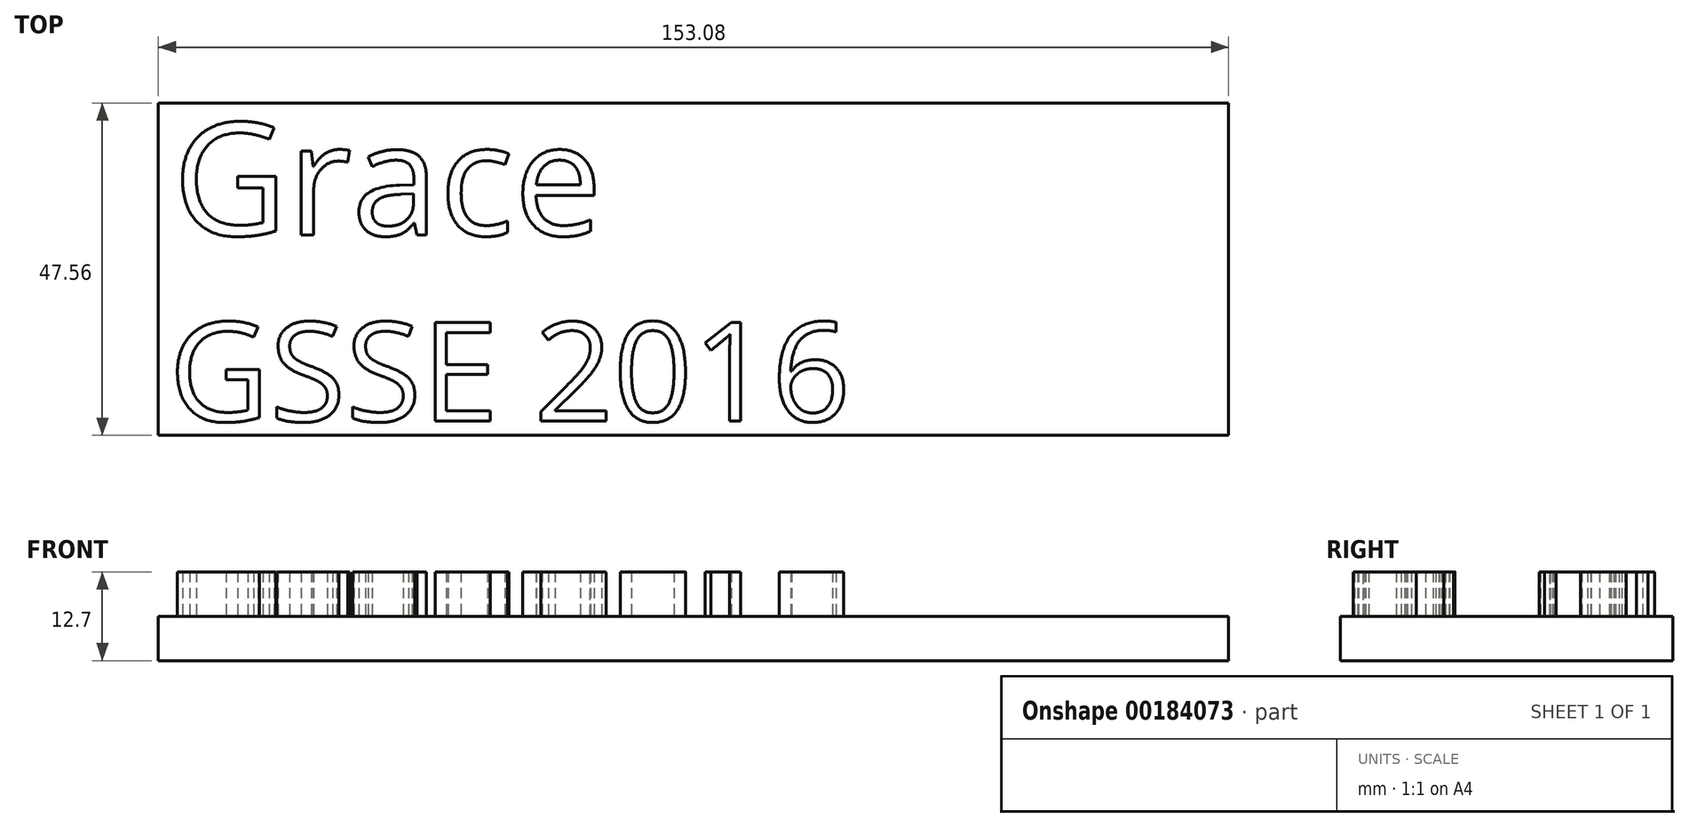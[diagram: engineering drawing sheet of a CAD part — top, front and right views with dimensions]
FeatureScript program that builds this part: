
annotation { "Feature Type Name" : "Feature", "Feature Type Description" : "" }
export const myFeature = defineFeature(function(context is Context, id is Id, definition is map)
    precondition{}
    {
        {
            var Q0;
            Q0=qCreatedBy(makeId("Top.planeOp"),FACE);
            var sketch = newSketch(context, id + "F0", { "sketchPlane" : qUnion([Q0])});
            skLineSegment(sketch, "E0.bottom", {"start": v(-76.54, 23.78) * mm, "end": v(76.54, 23.78) * mm});
            skLineSegment(sketch, "E0.top", {"start": v(-76.54, -23.78) * mm, "end": v(76.54, -23.78) * mm});
            skLineSegment(sketch, "E0.left", {"start": v(-76.54, 23.78) * mm, "end": v(-76.54, -23.78) * mm});
            skLineSegment(sketch, "E0.right", {"start": v(76.54, 23.78) * mm, "end": v(76.54, -23.78) * mm});
            skPoint(sketch, "E0.middle", {"position": v(0, 0) * mm});
            skSolve(sketch);
        }
        {
            var Q0;
            Q0 = qSketchRegion(id + "F0", true);
            extrude(context, id + "F1", {"entities" : qUnion([Q0]), "depth" : 6.35 * mm});
        }
        {
            var Q0;
            Q0=makeQuery(id+"F1.opExtrude","CAP_FACE",FACE,{"disambiguationData":[OSD([sQuery(id+"F0.wireOp",EDGE,"E0.bottom"),sQuery(id+"F0.wireOp",EDGE,"E0.top"),sQuery(id+"F0.wireOp",EDGE,"E0.left"),sQuery(id+"F0.wireOp",EDGE,"E0.right")])],"isStart":false});
            var sketch = newSketch(context, id + "F2", { "sketchPlane" : qUnion([Q0])});
            skText(sketch, "E1", { "text": "GSSE 2016", "fontName": "OpenSans-Regular.ttf"});
            const initialGuessF2  = {"E1": [-0.07502, -0.02174, 1, 0, 0.01424]};
            skSetInitialGuess(sketch, initialGuessF2);
            skSolve(sketch);
        }
        {
            var Q0;
            Q0 = qSketchRegion(id + "F2", true);
            extrude(context, id + "F3", {"entities" : qUnion([Q0]), "operationType" : NewBodyOperationType.ADD, "depth" : 6.35 * mm});
        }
        {
            var Q0;
            {var subQ34=sQuery(id+"F0.wireOp",EDGE,"E0.left");var subQ59=sQuery(id+"F0.wireOp",EDGE,"E0.bottom");var subQ67=sQuery(id+"F0.wireOp",EDGE,"E0.right");var subQ80=sQuery(id+"F0.wireOp",EDGE,"E0.top");Q0=makeQuery(id+"F3.boolean.opBoolean","SPLIT",FACE,{"disambiguationData":[TD([makeQuery(id+"F1.opExtrude","SWEPT_FACE",FACE,{"disambiguationData":[OSD([subQ59])]})])],"derivedFrom":makeQuery(id+"F1.opExtrude","CAP_FACE",FACE,{"disambiguationData":[OSD([subQ59,subQ80,subQ34,subQ67])],"isStart":false})});}
            var sketch = newSketch(context, id + "F4", { "sketchPlane" : qUnion([Q0])});
            skText(sketch, "E2", { "text": "Grace", "fontName": "OpenSans-Regular.ttf"});
            const initialGuessF4  = {"E2": [-0.07446, 0.00486, 1, 0, 0.0162]};
            skSetInitialGuess(sketch, initialGuessF4);
            skSolve(sketch);
        }
        {
            var Q0;
            Q0 = qSketchRegion(id + "F4", true);
            extrude(context, id + "F5", {"entities" : qUnion([Q0]), "operationType" : NewBodyOperationType.ADD, "depth" : 6.35 * mm});
        }
    });
